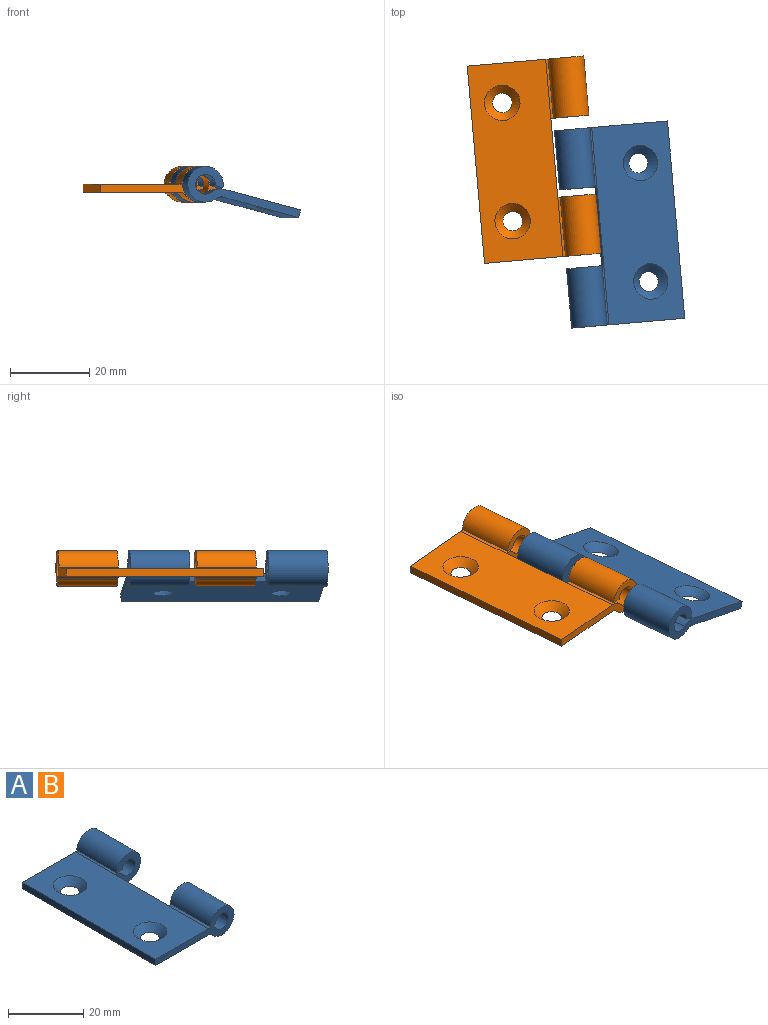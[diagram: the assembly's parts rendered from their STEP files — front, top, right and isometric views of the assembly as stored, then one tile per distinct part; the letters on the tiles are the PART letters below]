
ASSEMBLY  parts=2 mates=1
PART A: 20 faces, bbox 29.5x50x9 mm
  f0: cylinder r=4mm len=15mm, axis (0,-1,0), area 54.5mm2, adj f4,f6,f13,f16
  f1: cylinder r=2mm len=15mm, axis (0,-1,0), area 27.2mm2, adj f2,f8,f13,f16
  f2: cylinder r=4.5mm len=15mm, axis (0,-1,0), area 374.9mm2, adj f1,f3,f13,f16
  f3: plane 15x2.01mm, normal (0,0,-1), area 30.1mm2, adj f2,f4,f13,f16
  f4: cylinder r=2.5mm len=15mm, axis (0,-1,0), area 206.3mm2, adj f0,f3,f13,f16
  f5: cylinder r=4mm len=15mm, axis (0,-1,0), area 54.5mm2, adj f6,f12,f14,f17
  f6: plane 50x19.88mm, normal (0,0,1), area 867.7mm2, adj f0,f5,f7,f13,f14,f15,f18,f19
  f7: plane 50x2mm, normal (-1,0,0), area 100mm2, adj f6,f8,f13,f14
  f8: plane 50x19.88mm, normal (0,0,-1), area 955.2mm2, adj f1,f7,f9,f13,f14,f15,f18,f19
  f9: cylinder r=2mm len=15mm, axis (0,-1,0), area 27.2mm2, adj f8,f10,f14,f17
  f10: cylinder r=4.5mm len=15mm, axis (0,-1,0), area 374.9mm2, adj f9,f11,f14,f17
  f11: plane 15x2.01mm, normal (0,0,-1), area 30.1mm2, adj f10,f12,f14,f17
  f12: cylinder r=2.5mm len=15mm, axis (0,-1,0), area 206.3mm2, adj f5,f11,f14,f17
  f13: plane 29.5x9mm, normal (0,1,0), area 83.9mm2, adj f0,f1,f2,f3,f4,f6,f7,f8
  f14: plane 29.5x9mm, normal (0,-1,0), area 83.9mm2, adj f5,f6,f7,f8,f9,f10,f11,f12
  f15: plane 20x2mm, normal (1,0,0), area 40mm2, adj f6,f8,f16,f17
  f16: plane 9.62x9mm, normal (0,-1,0), area 44.2mm2, adj f0,f1,f2,f3,f4,f15
  f17: plane 9.62x9mm, normal (0,1,0), area 44.2mm2, adj f5,f9,f10,f11,f12,f15
  f18: cone r=2.25mm half-angle=45deg, axis (0,0,1), area 61.8mm2, adj f6,f8
  f19: cone r=2.25mm half-angle=45deg, axis (0,0,1), area 61.8mm2, adj f6,f8
PART B: same geometry as A
PLACE A rot(axis=(-0.13,-0.01,-0.99),175deg) t=(26.51,8.22,17.58)mm
PLACE B rot(axis=(0,0,1),5deg) t=(29.28,-23.47,17.58)mm
MATE cylindrical B.f2 <-> A.f2  axis (0.09,-1,0) through (28.63,-15.99,17.58)mm
